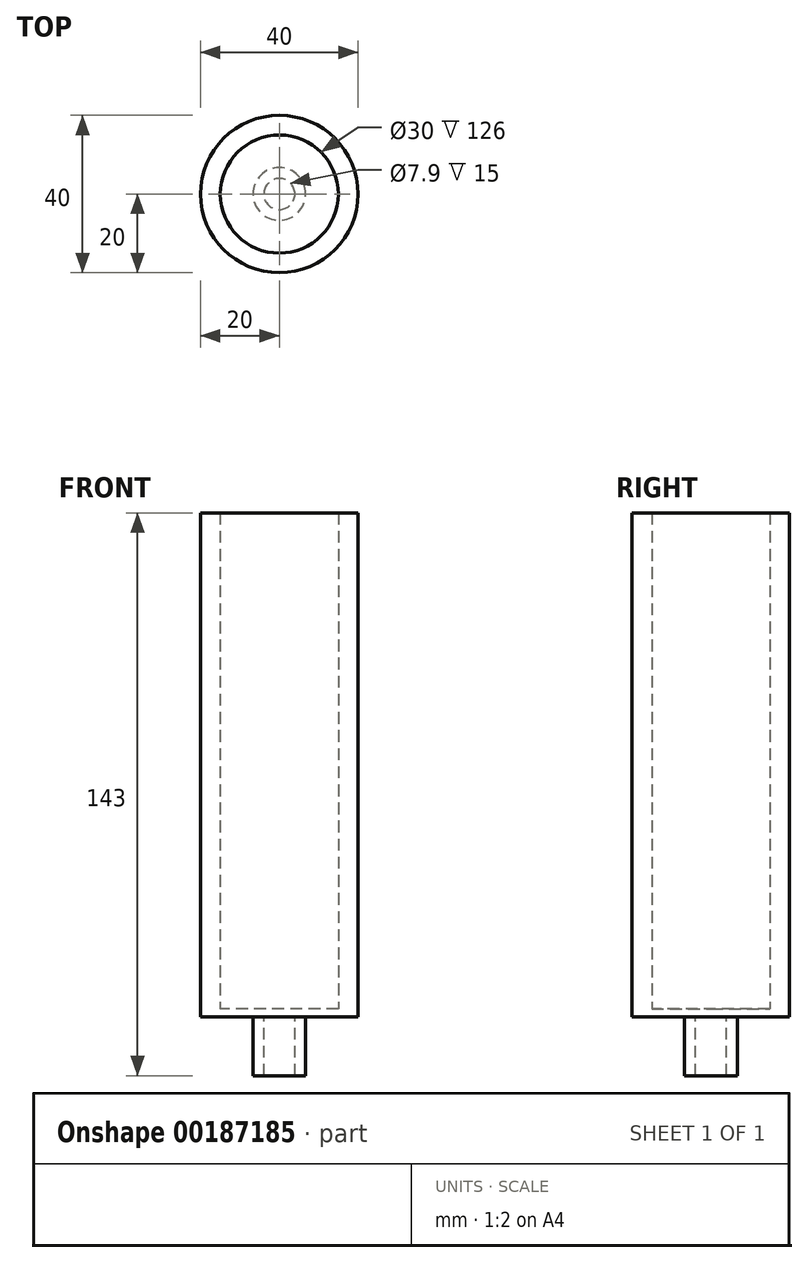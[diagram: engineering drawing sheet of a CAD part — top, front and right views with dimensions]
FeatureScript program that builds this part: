
annotation { "Feature Type Name" : "Feature", "Feature Type Description" : "" }
export const myFeature = defineFeature(function(context is Context, id is Id, definition is map)
    precondition{}
    {
        {
            var Q0;
            Q0=qCreatedBy(makeId("Top.planeOp"),FACE);
            var sketch = newSketch(context, id + "F0", { "sketchPlane" : qUnion([Q0])});
            skCircle(sketch, "E0", {"center": v(0, 0) * mm, "radius": 15 * mm});
            skCircle(sketch, "E1", {"center": v(0, 0) * mm, "radius": 20 * mm});
            skSolve(sketch);
        }
        {
            var Q0;
            Q0=makeQuery(id+"F0.imprint","IMPRINT",FACE,{"disambiguationData":[TD([[makeQuery(id+"F0.imprint","IMPRINT",EDGE,{"derivedFrom":sQuery(id+"F0.wireOp",EDGE,"E0")}),-1.0]])]});
            extrude(context, id + "F1", {"entities" : qUnion([Q0]), "depth" : 126 * mm});
        }
        {
            var Q0;
            Q0=makeQuery(id+"F1.opExtrude","CAP_FACE",FACE,{"disambiguationData":[OSD([sQuery(id+"F0.wireOp",EDGE,"E0"),sQuery(id+"F0.wireOp",EDGE,"E1")])],"isStart":true});
            var sketch = newSketch(context, id + "F2", { "sketchPlane" : qUnion([Q0])});
            skCircle(sketch, "E2", {"center": v(0, 0) * mm, "radius": 20 * mm});
            skSolve(sketch);
        }
        {
            var Q0;
            Q0 = qSketchRegion(id + "F2", true);
            extrude(context, id + "F3", {"entities" : qUnion([Q0]), "operationType" : NewBodyOperationType.ADD, "depth" : 2 * mm});
        }
        {
            var Q0;
            Q0=makeQuery(id+"F3.opExtrude","CAP_FACE",FACE,{"disambiguationData":[OSD([sQuery(id+"F2.wireOp",EDGE,"E2")])],"isStart":false});
            var sketch = newSketch(context, id + "F4", { "sketchPlane" : qUnion([Q0])});
            skCircle(sketch, "E3", {"center": v(0, 0) * mm, "radius": 3.95 * mm});
            skCircle(sketch, "E4", {"center": v(0, 0) * mm, "radius": 6.7 * mm});
            skSolve(sketch);
        }
        {
            var Q0;
            Q0 = qSketchRegion(id + "F4", true);
            extrude(context, id + "F5", {"entities" : qUnion([Q0]), "operationType" : NewBodyOperationType.ADD, "depth" : 15 * mm});
        }
    });
